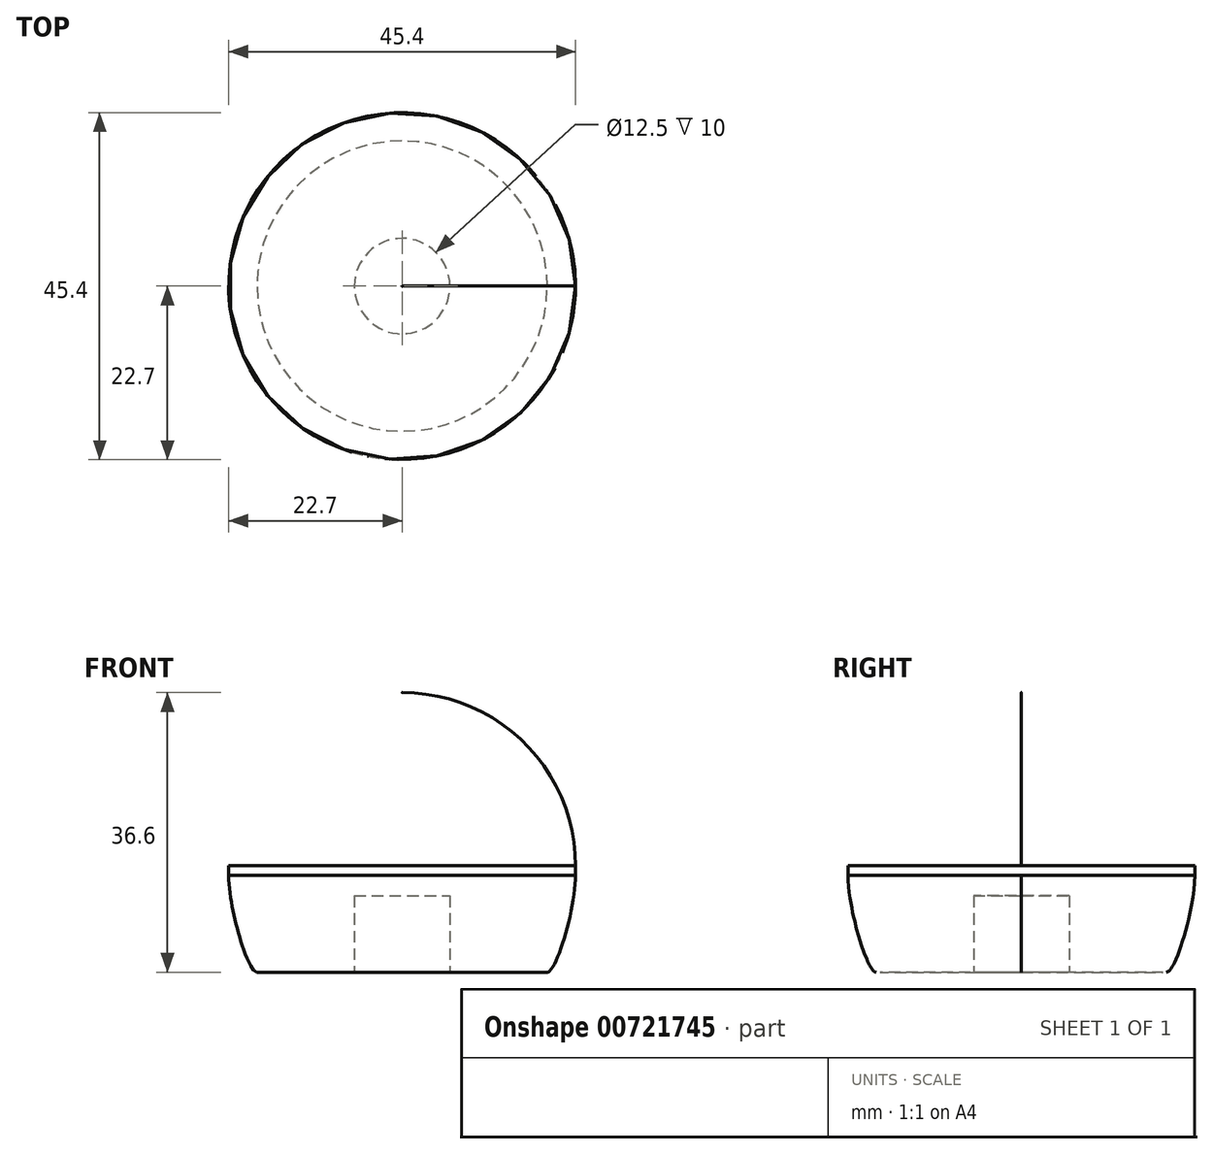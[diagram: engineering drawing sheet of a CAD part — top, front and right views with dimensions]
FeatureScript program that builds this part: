
annotation { "Feature Type Name" : "Feature", "Feature Type Description" : "" }
export const myFeature = defineFeature(function(context is Context, id is Id, definition is map)
    precondition{}
    {
        {
            var Q0;
            Q0=qCreatedBy(makeId("Top.planeOp"),FACE);
            var sketch = newSketch(context, id + "F0", { "sketchPlane" : qUnion([Q0])});
            skCircle(sketch, "E0", {"center": v(0, 0) * mm, "radius": 19 * mm});
            skSolve(sketch);
        }
        {
            var Q0;
            Q0=qCreatedBy(makeId("Top.planeOp"),FACE);
            cPlane(context, id + "F1", {"entities" : qUnion([Q0]), "cplaneType" : CPlaneType.OFFSET, "offset" : 12.7 * mm, "width" : 150 * mm, "height" : 150 * mm});
        }
        {
            var Q0;
            Q0=qCreatedBy(id+"F1.planeOp",FACE);
            var sketch = newSketch(context, id + "F2", { "sketchPlane" : qUnion([Q0])});
            skCircle(sketch, "E1", {"center": v(0, 0) * mm, "radius": 22.7 * mm});
            skSolve(sketch);
        }
        {
            var Q0;
            Q0=makeQuery(id+"F0.imprint","IMPRINT",FACE,{"disambiguationData":[TD([[makeQuery(id+"F0.imprint","IMPRINT",EDGE,{"derivedFrom":sQuery(id+"F0.wireOp",EDGE,"E0")}),1.0]])]});
            var Q1;
            Q1=makeQuery(id+"F2.imprint","IMPRINT",FACE,{"disambiguationData":[TD([[makeQuery(id+"F2.imprint","IMPRINT",EDGE,{"derivedFrom":sQuery(id+"F2.wireOp",EDGE,"E1")}),1.0]])]});
            loft(context, id + "F3", {"startCondition" : LoftEndDerivativeType.TANGENT_TO_PROFILE, "startMagnitude" : 1, "endCondition" : LoftEndDerivativeType.NORMAL_TO_PROFILE, "endMagnitude" : 1, "sheetProfilesArray" : [{ "sheetProfileEntities" : qUnion([Q0]) }, { "sheetProfileEntities" : qUnion([Q1]) }]});
        }
        {
            var Q0;
            Q0=qCreatedBy(id+"F1.planeOp",FACE);
            cPlane(context, id + "F4", {"entities" : qUnion([Q0]), "cplaneType" : CPlaneType.OFFSET, "offset" : 23.9 * mm, "width" : 150 * mm, "height" : 150 * mm});
        }
        {
            var Q0;
            Q0=makeQuery(id+"F3.opLoft","CAP_FACE",FACE,{"disambiguationData":[OSD([makeQuery(id+"F2.imprint","IMPRINT",FACE,{"disambiguationData":[TD([[makeQuery(id+"F2.imprint","IMPRINT",EDGE,{"derivedFrom":sQuery(id+"F2.wireOp",EDGE,"E1")}),1.0]])]})])],"isStart":true});
            var Q1;
            Q1=qCreatedBy(id+"F4.planeOp",FACE);
            extrude(context, id + "F5", {"entities" : qUnion([Q0]), "operationType" : NewBodyOperationType.ADD, "endBound" : BoundingType.UP_TO_SURFACE, "depth" : 14.7 * mm, "endBoundEntityFace" : qUnion([Q1]), "offsetDistance" : 25 * mm});
        }
        {
            var Q0;
            Q0=makeQuery(id+"F5.opExtrude","CAP_FACE",FACE,{"disambiguationData":[OSD([makeQuery(id+"F2.imprint","IMPRINT",FACE,{"disambiguationData":[TD([[makeQuery(id+"F2.imprint","IMPRINT",EDGE,{"derivedFrom":sQuery(id+"F2.wireOp",EDGE,"E1")}),1.0]])]})])],"isStart":false});
            fillet(context, id + "F6", {"entities" : qUnion([Q0]), "radius" : 22.67 * mm, "tangentPropagation" : true, "allowEdgeOverflow" : false});
        }
        {
            var Q0;
            Q0=makeQuery(id+"F3.opLoft","CAP_FACE",FACE,{"disambiguationData":[OSD([makeQuery(id+"F0.imprint","IMPRINT",FACE,{"disambiguationData":[TD([[makeQuery(id+"F0.imprint","IMPRINT",EDGE,{"derivedFrom":sQuery(id+"F0.wireOp",EDGE,"E0")}),1.0]])]})])],"isStart":true});
            var sketch = newSketch(context, id + "F7", { "sketchPlane" : qUnion([Q0])});
            skCircle(sketch, "E2", {"center": v(0, 0) * mm, "radius": 6.25 * mm});
            skSolve(sketch);
        }
        {
            var Q0;
            Q0=makeQuery(id+"F7.imprint","IMPRINT",FACE,{"disambiguationData":[TD([[makeQuery(id+"F7.imprint","IMPRINT",EDGE,{"derivedFrom":sQuery(id+"F7.wireOp",EDGE,"E2")}),1.0]])]});
            extrude(context, id + "F8", {"entities" : qUnion([Q0]), "operationType" : NewBodyOperationType.REMOVE, "oppositeDirection" : true, "depth" : 10 * mm, "offsetDistance" : 25 * mm});
        }
    });
